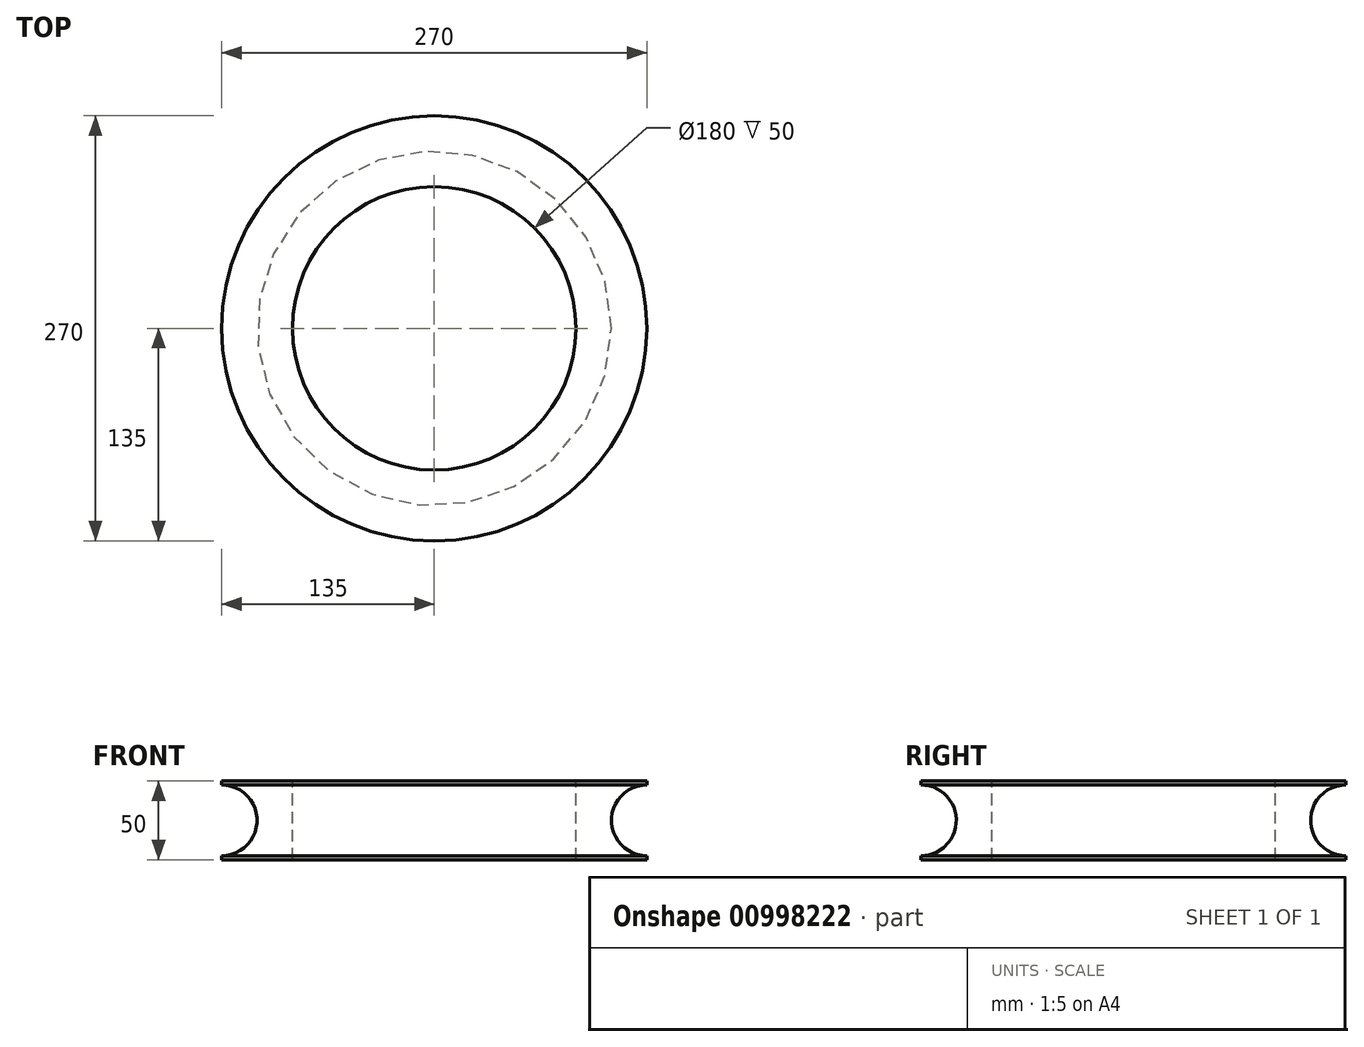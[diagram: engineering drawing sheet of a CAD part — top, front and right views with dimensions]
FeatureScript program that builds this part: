
annotation { "Feature Type Name" : "Feature", "Feature Type Description" : "" }
export const myFeature = defineFeature(function(context is Context, id is Id, definition is map)
    precondition{}
    {
        {
            var Q0;
            Q0=qCreatedBy(makeId("Front.planeOp"),FACE);
            var sketch = newSketch(context, id + "F0", { "sketchPlane" : qUnion([Q0])});
            skLineSegment(sketch, "E0.bottom", {"start": v(22.5, 25) * mm, "end": v(-22.5, 25) * mm});
            skLineSegment(sketch, "E0.top", {"start": v(22.5, -25) * mm, "end": v(-22.5, -25) * mm});
            skLineSegment(sketch, "E0.left", {"start": v(22.5, 25) * mm, "end": v(22.5, 22.5) * mm});
            skLineSegment(sketch, "E0.right", {"start": v(-22.5, 25) * mm, "end": v(-22.5, -25) * mm});
            skPoint(sketch, "E0.middle", {"position": v(0, 0) * mm});
            skArc(sketch, "E1", {"start": v(22.5, 22.5) * mm, "mid": v(0, 0) * mm, "end": v(22.5, -22.5) * mm});
            skPoint(sketch, "E1.second.point", {"position": v(22.5, 22.5) * mm});
            skPoint(sketch, "E1.third.point", {"position": v(22.5, -22.5) * mm});
            skLineSegment(sketch, "E2.trimOffspring", {"start": v(22.5, -22.5) * mm, "end": v(22.5, -25) * mm});
            skLineSegment(sketch, "E3", {"start": v(6.92, 22.5) * mm, "end": v(45.5, 22.5) * mm, "construction": true});
            skLineSegment(sketch, "E4", {"start": v(0, 0) * mm, "end": v(22.5, 0) * mm, "construction": true});
            skLineSegment(sketch, "E5", {"start": v(22.5, 22.5) * mm, "end": v(22.5, -22.5) * mm, "construction": true});
            skSolve(sketch);
        }
        {
            var Q0;
            Q0=qCreatedBy(makeId("Front.planeOp"),FACE);
            var sketch = newSketch(context, id + "F1", { "sketchPlane" : qUnion([Q0])});
            skLineSegment(sketch, "E6", {"start": v(-112.5, 109.06) * mm, "end": v(-112.5, -118.8) * mm});
            skSolve(sketch);
        }
        {
            var Q0;
            Q0=makeQuery(id+"F0.imprint","IMPRINT",FACE,{"disambiguationData":[TD([[makeQuery(id+"F0.imprint","IMPRINT",EDGE,{"derivedFrom":sQuery(id+"F0.wireOp",EDGE,"E0.bottom")}),1.0]])]});
            var Q1;
            Q1=sQuery(id+"F1.wireOp",EDGE,"E6");
            revolve(context, id + "F2", {"surfaceOperationType" : NewSurfaceOperationType.NEW, "entities" : qUnion([Q0]), "axis" : qUnion([Q1]), "revolveType" : RevolveType.FULL});
        }
    });
